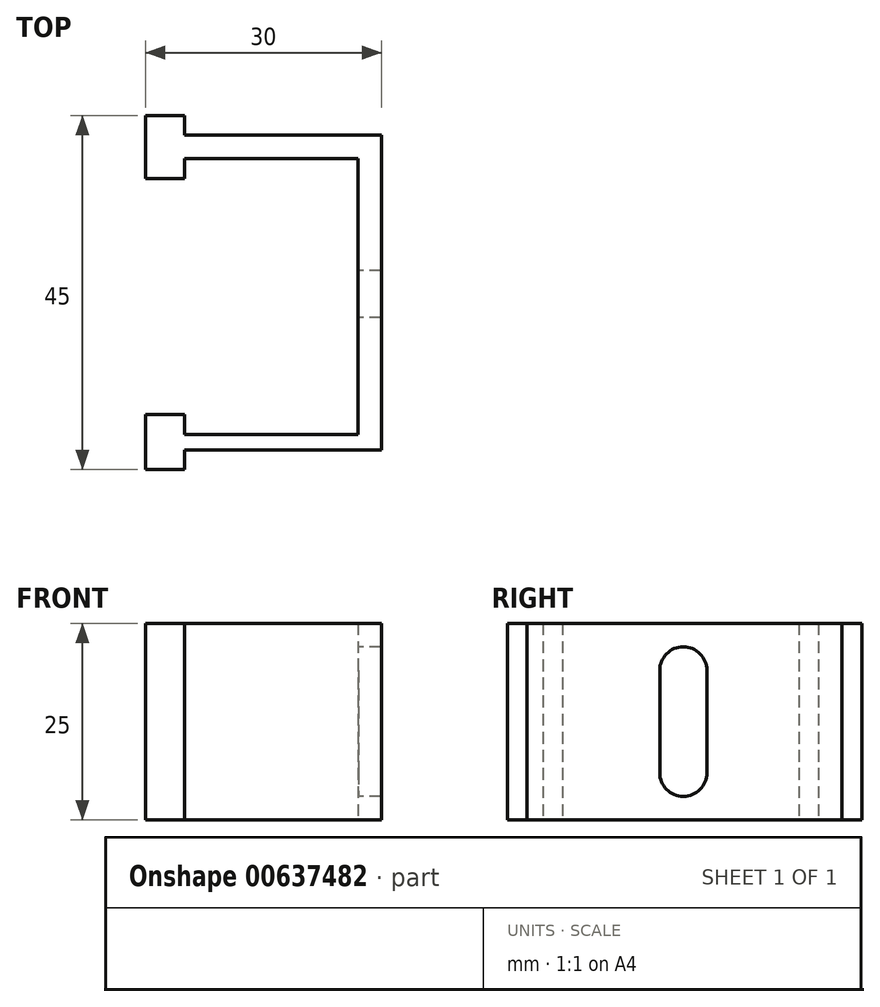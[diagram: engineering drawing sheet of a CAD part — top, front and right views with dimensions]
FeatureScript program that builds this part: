
annotation { "Feature Type Name" : "Feature", "Feature Type Description" : "" }
export const myFeature = defineFeature(function(context is Context, id is Id, definition is map)
    precondition{}
    {
        {
            var Q0;
            Q0=qCreatedBy(makeId("Top.planeOp"),FACE);
            var sketch = newSketch(context, id + "F0", { "sketchPlane" : qUnion([Q0])});
            skLineSegment(sketch, "E0", {"start": v(-22.05, 0.05) * mm, "end": v(-27.05, 0.05) * mm});
            skLineSegment(sketch, "E1", {"start": v(-27.05, 0.05) * mm, "end": v(-27.05, -6.95) * mm});
            skLineSegment(sketch, "E2", {"start": v(-27.05, -6.95) * mm, "end": v(-22.05, -6.95) * mm});
            skLineSegment(sketch, "E3", {"start": v(-22.05, -6.95) * mm, "end": v(-22.05, -4.45) * mm});
            skLineSegment(sketch, "E4", {"start": v(-22.05, -4.45) * mm, "end": v(2.95, -4.45) * mm});
            skLineSegment(sketch, "E5", {"start": v(2.95, -4.45) * mm, "end": v(2.95, 35.55) * mm});
            skLineSegment(sketch, "E6", {"start": v(2.95, 35.55) * mm, "end": v(-22.05, 35.55) * mm});
            skLineSegment(sketch, "E7", {"start": v(-22.05, 35.55) * mm, "end": v(-22.05, 38.05) * mm});
            skLineSegment(sketch, "E8", {"start": v(-22.05, 38.05) * mm, "end": v(-27.05, 38.05) * mm});
            skLineSegment(sketch, "E9", {"start": v(-27.05, 38.05) * mm, "end": v(-27.05, 30.05) * mm});
            skLineSegment(sketch, "E10", {"start": v(-27.05, 30.05) * mm, "end": v(-22.05, 30.05) * mm});
            skLineSegment(sketch, "E11", {"start": v(-22.05, 30.05) * mm, "end": v(-22.05, 32.55) * mm});
            skLineSegment(sketch, "E12", {"start": v(-22.05, 32.55) * mm, "end": v(-0.05, 32.55) * mm});
            skLineSegment(sketch, "E13", {"start": v(-0.05, 32.55) * mm, "end": v(-0.05, -2.45) * mm});
            skLineSegment(sketch, "E14", {"start": v(-0.05, -2.45) * mm, "end": v(-22.05, -2.45) * mm});
            skLineSegment(sketch, "E15", {"start": v(-22.05, -2.45) * mm, "end": v(-22.05, 0.05) * mm});
            skSolve(sketch);
        }
        {
            var Q0;
            Q0 = qSketchRegion(id + "F0", true);
            extrude(context, id + "F1", {"entities" : qUnion([Q0]), "depth" : 25 * mm, "offsetDistance" : 25 * mm});
        }
        {
            var Q0;
            Q0=qCreatedBy(makeId("Right.planeOp"),FACE);
            var sketch = newSketch(context, id + "F2", { "sketchPlane" : qUnion([Q0])});
            skArc(sketch, "E16", {"start": v(18.38, 19) * mm, "mid": v(15.38, 22) * mm, "end": v(12.38, 19) * mm});
            skArc(sketch, "E17", {"start": v(12.38, 6) * mm, "mid": v(15.38, 3) * mm, "end": v(18.38, 6) * mm});
            skLineSegment(sketch, "E18", {"start": v(12.38, 19) * mm, "end": v(12.38, 6) * mm});
            skLineSegment(sketch, "E19", {"start": v(18.38, 6) * mm, "end": v(18.38, 19) * mm});
            skSolve(sketch);
        }
        {
            var Q0;
            Q0 = qSketchRegion(id + "F2", true);
            var Q1;
            Q1=sQuery(id+"F2.wireOp",EDGE,"E16");
            var Q2;
            Q2=sQuery(id+"F2.wireOp",EDGE,"E18");
            var Q3;
            Q3=sQuery(id+"F2.wireOp",EDGE,"E17");
            extrude(context, id + "F3", {"entities" : qUnion([Q0]), "operationType" : NewBodyOperationType.REMOVE, "surfaceEntities" : qUnion([Q1, Q2, Q3]), "depth" : 25 * mm, "offsetDistance" : 25 * mm});
        }
    });
